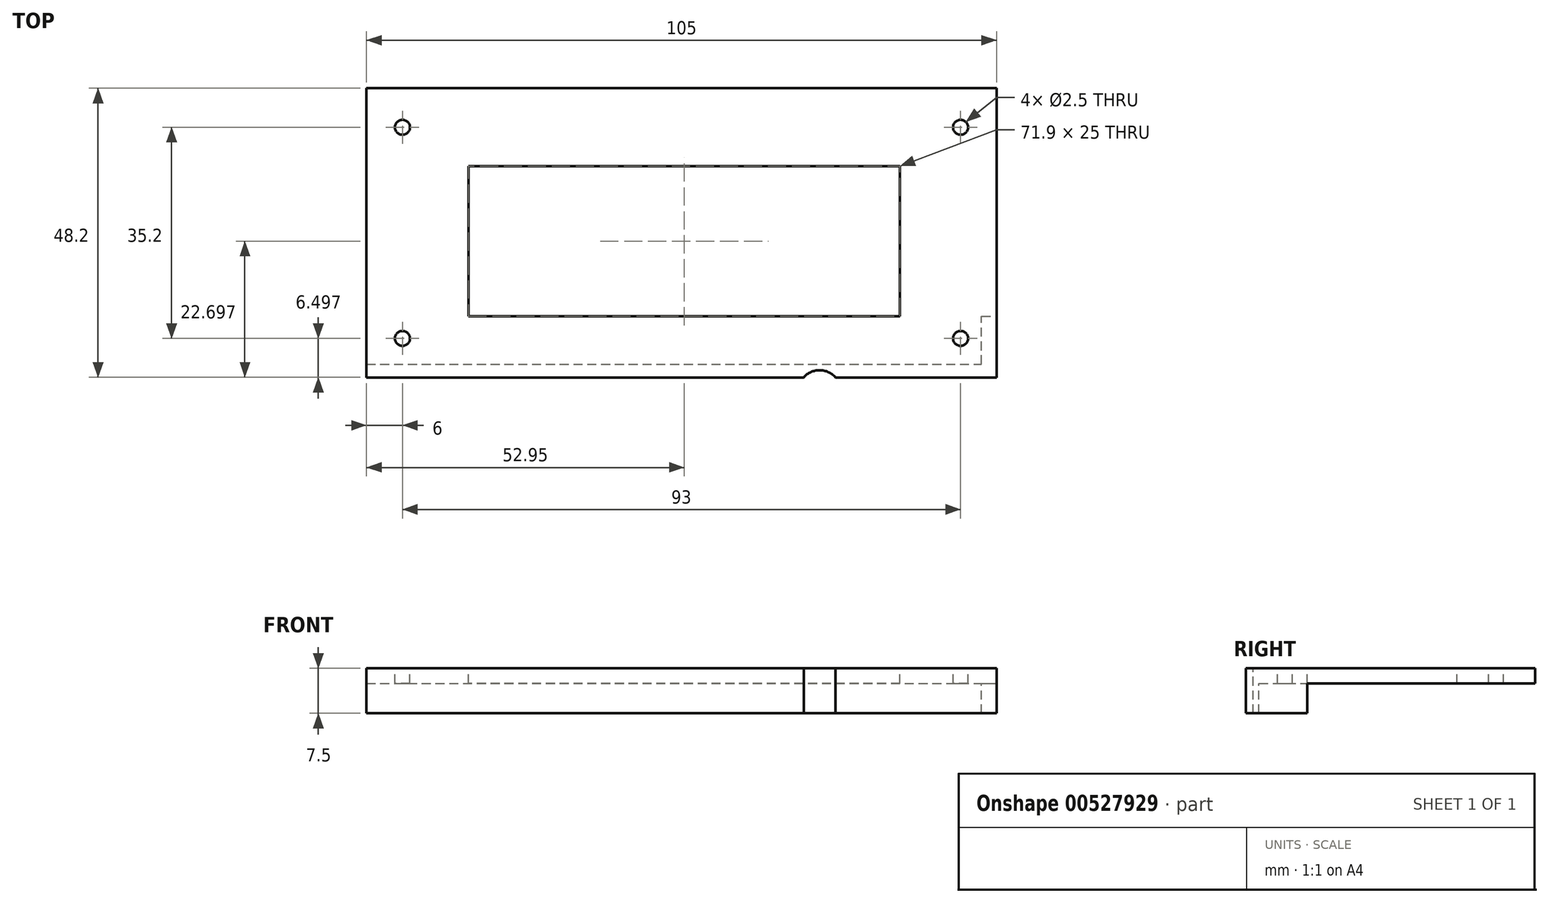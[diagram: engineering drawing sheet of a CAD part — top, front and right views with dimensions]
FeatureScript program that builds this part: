
annotation { "Feature Type Name" : "Feature", "Feature Type Description" : "" }
export const myFeature = defineFeature(function(context is Context, id is Id, definition is map)
    precondition{}
    {
        {
            var Q0;
            Q0=qCreatedBy(makeId("Right.planeOp"),FACE);
            var sketch = newSketch(context, id + "F0", { "sketchPlane" : qUnion([Q0])});
            skLineSegment(sketch, "E0", {"start": v(-24.63, 10.69) * mm, "end": v(-24.63, 15.69) * mm});
            skLineSegment(sketch, "E1", {"start": v(-24.63, 15.69) * mm, "end": v(21.37, 15.69) * mm});
            skLineSegment(sketch, "E2", {"start": v(21.37, 15.69) * mm, "end": v(21.37, 18.19) * mm});
            skLineSegment(sketch, "E3", {"start": v(21.37, 18.19) * mm, "end": v(-26.83, 18.19) * mm});
            skLineSegment(sketch, "E4", {"start": v(-26.83, 18.19) * mm, "end": v(-26.83, 10.69) * mm});
            skLineSegment(sketch, "E5", {"start": v(-26.83, 10.69) * mm, "end": v(-24.63, 10.69) * mm});
            skLineSegment(sketch, "E6", {"start": v(-24.63, 15.69) * mm, "end": v(-26.83, 15.69) * mm});
            skPoint(sketch, "E6.endSnap0", {"position": v(-26.83, 14.44) * mm});
            skLineSegment(sketch, "E7", {"start": v(-24.63, 10.69) * mm, "end": v(-16.63, 10.69) * mm});
            skLineSegment(sketch, "E8", {"start": v(-16.63, 10.69) * mm, "end": v(-16.63, 15.69) * mm});
            skSolve(sketch);
        }
        {
            var Q0;
            Q0=makeQuery(id+"F0.imprint","IMPRINT",FACE,{"disambiguationData":[TD([[makeQuery(id+"F0.imprint","IMPRINT",EDGE,{"derivedFrom":sQuery(id+"F0.wireOp",EDGE,"E0")}),1.0]])]});
            var Q1;
            {var subQ1=sQuery(id+"F0.wireOp",EDGE,"E2");Q1=makeQuery(id+"F0.imprint","IMPRINT",FACE,{"disambiguationData":[TD([[makeQuery(id+"F0.imprint","IMPRINT",EDGE,{"derivedFrom":subQ1}),1.0]])]});}
            extrude(context, id + "F1", {"entities" : qUnion([Q0, Q1]), "oppositeDirection" : true, "depth" : 105 * mm, "offsetDistance" : 25 * mm});
        }
        {
            var Q0;
            Q0=makeQuery(id+"F1.opExtrude","SWEPT_FACE",FACE,{"disambiguationData":[OSD([sQuery(id+"F0.wireOp",EDGE,"E3")])]});
            var sketch = newSketch(context, id + "F2", { "sketchPlane" : qUnion([Q0])});
            skCircle(sketch, "E9", {"center": v(-99, 14.87) * mm, "radius": 1.25 * mm});
            skCircle(sketch, "E10", {"center": v(-99, -20.33) * mm, "radius": 1.25 * mm});
            skCircle(sketch, "E11", {"center": v(-6, 14.87) * mm, "radius": 1.25 * mm});
            skCircle(sketch, "E12", {"center": v(-6, -20.33) * mm, "radius": 1.25 * mm});
            skSolve(sketch);
        }
        {
            var Q0;
            Q0=makeQuery(id+"F2.imprint","IMPRINT",FACE,{"disambiguationData":[TD([[makeQuery(id+"F2.imprint","IMPRINT",EDGE,{"derivedFrom":sQuery(id+"F2.wireOp",EDGE,"E9")}),1.0]])]});
            var Q1;
            Q1=makeQuery(id+"F2.imprint","IMPRINT",FACE,{"disambiguationData":[TD([[makeQuery(id+"F2.imprint","IMPRINT",EDGE,{"derivedFrom":sQuery(id+"F2.wireOp",EDGE,"E11")}),1.0]])]});
            var Q2;
            Q2=makeQuery(id+"F2.imprint","IMPRINT",FACE,{"disambiguationData":[TD([[makeQuery(id+"F2.imprint","IMPRINT",EDGE,{"derivedFrom":sQuery(id+"F2.wireOp",EDGE,"E12")}),1.0]])]});
            var Q3;
            Q3=makeQuery(id+"F2.imprint","IMPRINT",FACE,{"disambiguationData":[TD([[makeQuery(id+"F2.imprint","IMPRINT",EDGE,{"derivedFrom":sQuery(id+"F2.wireOp",EDGE,"E10")}),1.0]])]});
            extrude(context, id + "F3", {"entities" : qUnion([Q0, Q1, Q2, Q3]), "operationType" : NewBodyOperationType.REMOVE, "oppositeDirection" : true, "depth" : 2.5 * mm, "offsetDistance" : 25 * mm});
        }
        {
            var Q0;
            Q0=makeQuery(id+"F1.opExtrude","SWEPT_FACE",FACE,{"disambiguationData":[OSD([sQuery(id+"F0.wireOp",EDGE,"E3")])]});
            var sketch = newSketch(context, id + "F4", { "sketchPlane" : qUnion([Q0])});
            skLineSegment(sketch, "E13", {"start": v(-88, 8.37) * mm, "end": v(-16.1, 8.37) * mm});
            skLineSegment(sketch, "E14", {"start": v(-16.1, 8.37) * mm, "end": v(-16.1, -16.63) * mm});
            skLineSegment(sketch, "E15", {"start": v(-16.1, -16.63) * mm, "end": v(-88, -16.63) * mm});
            skLineSegment(sketch, "E16", {"start": v(-88, -16.63) * mm, "end": v(-88, 8.37) * mm});
            skCircle(sketch, "E17", {"center": v(-29.5, -29.13) * mm, "radius": 3.5 * mm});
            skSolve(sketch);
        }
        {
            var Q0;
            Q0=makeQuery(id+"F4.imprint","IMPRINT",FACE,{"disambiguationData":[TD([[makeQuery(id+"F4.imprint","IMPRINT",EDGE,{"derivedFrom":sQuery(id+"F4.wireOp",EDGE,"E13")}),-1.0]])]});
            var Q1;
            {var subQ0=sQuery(id+"F4.wireOp",EDGE,"E17");var subQ1=makeQuery(id+"F1.opExtrude","SWEPT_EDGE",EDGE,{"disambiguationData":[OSD([sQuery(id+"F0.wireOp",EDGE,"E3"),sQuery(id+"F0.wireOp",EDGE,"E4")])]});var subQ2=makeQuery(id+"F4.imprint","INTERSECT",VERTEX,{"disambiguationData":[OD(0.0)],"derivedFrom":[subQ1,subQ0]});Q1=makeQuery(id+"F4.imprint","IMPRINT",FACE,{"disambiguationData":[TD([[makeQuery(id+"F4.imprint","IMPRINT",EDGE,{"disambiguationData":[TD([[subQ2,-1.0]])],"derivedFrom":subQ0}),1.0]])]});}
            extrude(context, id + "F5", {"entities" : qUnion([Q0, Q1]), "operationType" : NewBodyOperationType.REMOVE, "oppositeDirection" : true, "depth" : 7.5 * mm, "offsetDistance" : 25 * mm});
        }
        {
            var Q0;
            {var subQ0=sQuery(id+"F0.wireOp",EDGE,"E0");Q0=makeQuery(id+"F0.imprint","IMPRINT",FACE,{"disambiguationData":[TD([[makeQuery(id+"F0.imprint","IMPRINT",EDGE,{"derivedFrom":subQ0}),-1.0]])]});}
            extrude(context, id + "F6", {"entities" : qUnion([Q0]), "operationType" : NewBodyOperationType.ADD, "oppositeDirection" : true, "depth" : 2.5 * mm, "offsetDistance" : 25 * mm});
        }
    });
